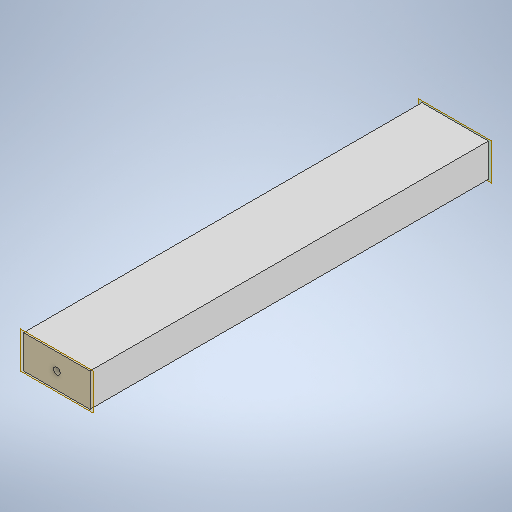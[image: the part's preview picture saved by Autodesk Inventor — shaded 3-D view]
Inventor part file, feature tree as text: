
AUTODESK INVENTOR PART (.ipt)
format: ipt  version: 2025.1 (Build 291241000, 241)  size: 230,400 bytes
history: native  units: mm
features: other x3, sketch x3, hole x2, extrude x1
ambient origin geometry x8: Origin, YZ Plane, XZ Plane, XY Plane, X Axis, Y Axis, Z Axis, Center Point
bodies: Body1 (feature_tree)
feature tree (9):
  other  "ソリッド1"
  extrude  "押し出し1"  Depth=50.0mm
  other  "作業平面1"
  sketch  "スケッチ2"
  other  "作業平面2"
  hole  "穴1"  [1 undecoded]
  hole  "穴2"  [1 undecoded]
  sketch  "スケッチ1"
  sketch  "スケッチ3"
note: 2 required parameter values undecoded (feature->parameter linkage not recoverable at this tier; creation-order binding heuristic only, values carry confidence <= 0.55)
